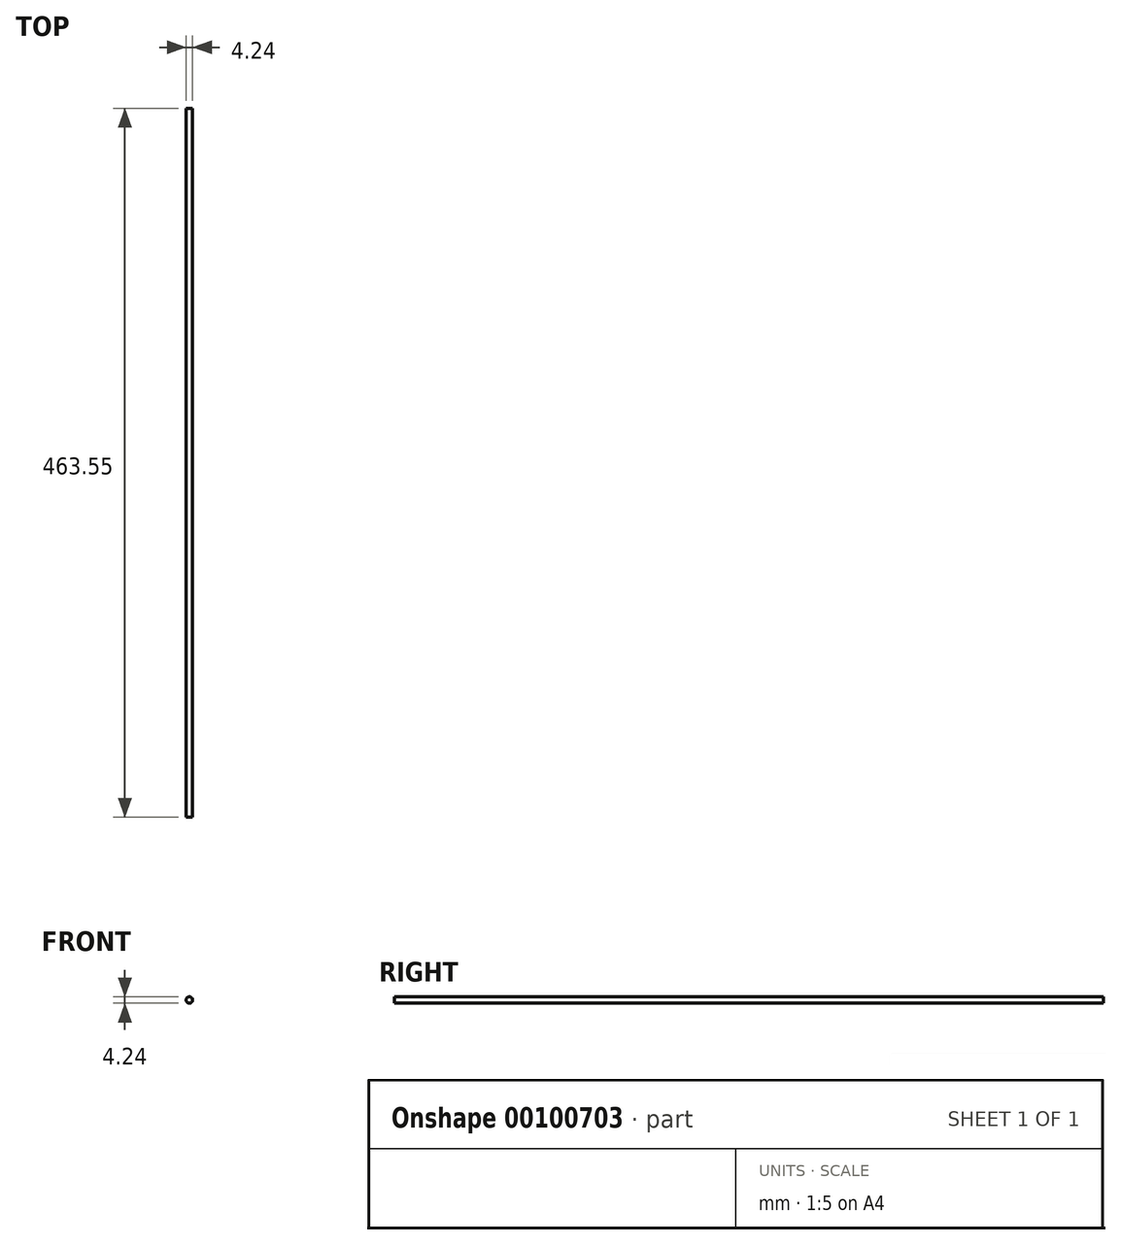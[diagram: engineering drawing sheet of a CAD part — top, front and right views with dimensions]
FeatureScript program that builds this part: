
annotation { "Feature Type Name" : "Feature", "Feature Type Description" : "" }
export const myFeature = defineFeature(function(context is Context, id is Id, definition is map)
    precondition{}
    {
        {
            var Q0;
            Q0=qCreatedBy(makeId("Front.planeOp"),FACE);
            var sketch = newSketch(context, id + "F1", { "sketchPlane" : qUnion([Q0])});
            skCircle(sketch, "E0", {"center": v(0, 0) * mm, "radius": 2.12 * mm});
            skSolve(sketch);
        }
        {
            var Q0;
            Q0 = qSketchRegion(id + "F1", true);
            extrude(context, id + "F0", {"entities" : qUnion([Q0]), "oppositeDirection" : true, "depth" : 463.55 * mm});
        }
    });
